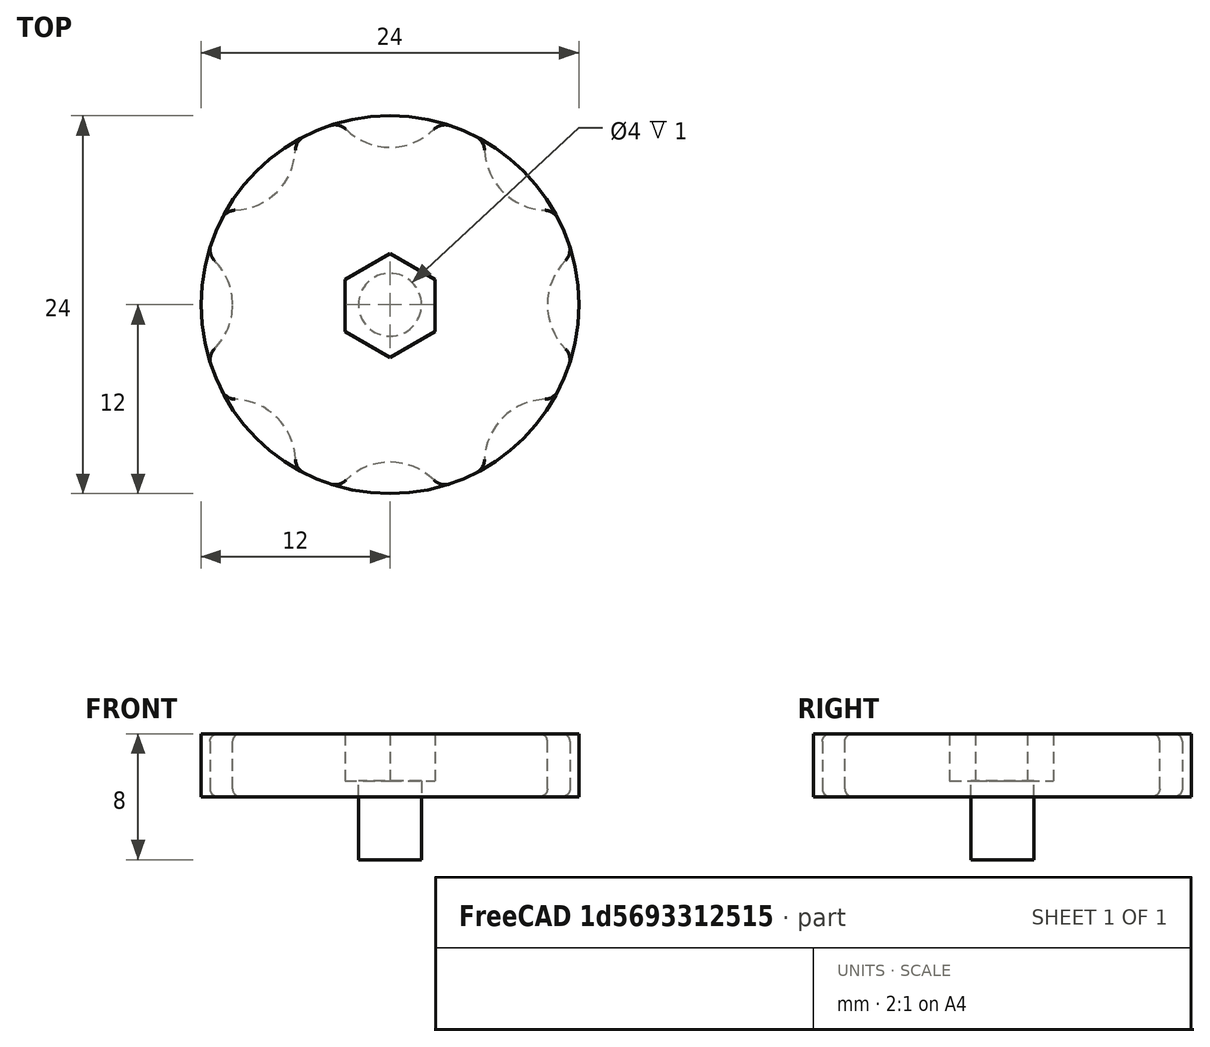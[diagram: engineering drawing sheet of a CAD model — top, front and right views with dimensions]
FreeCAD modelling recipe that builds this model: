
FCSTD DOCUMENT  (FreeCAD 0.15R4671 (Git))
Label: BedKnob
License: All rights reserved
LicenseURL: http://en.wikipedia.org/wiki/All_rights_reserved
objects: Sketcher::SketchObject×4, PartDesign::Pocket×3, PartDesign::Fillet×2, Mesh::Feature×1, PartDesign::Pad×1
note: 14 computed .brp shape members not serialized (recipe doc carries the construction recipe); baked Part::Feature solids carry a one-line shape summary decoded from their .brp

FEATURE [Mesh::Feature] HexNutStyle1_M3
  Placement = pos=(14.2,22,-115) rot=(0,0,1;0rad)
FEATURE [Sketcher::SketchObject] Sketch
  sketch-geometry (1):
    g0: Circle CenterX=0 CenterY=0 CenterZ=0 NormalX=0 NormalY=0 NormalZ=1 Radius=12
  constraints (1):
    c: Radius(g0) = 12
FEATURE [PartDesign::Pad] Pad
  Length = 4
  Length2 = 100
  Sketch = -> Sketch
  Type = 0
FEATURE [Sketcher::SketchObject] Sketch001
  Placement = pos=(0,0,4) rot=(0,0,1;0rad)
  Support = -> Pad [Face3]
  sketch-geometry (7):
    g0: LineSegment StartX=0 StartY=3.25 StartZ=0 EndX=-2.86084 EndY=1.59829 EndZ=0
    g1: LineSegment StartX=-2.86084 StartY=1.59829 StartZ=0 EndX=-2.86084 EndY=-1.70512 EndZ=0
    g2: LineSegment StartX=-2.86084 StartY=-1.70512 StartZ=0 EndX=0 EndY=-3.35682 EndZ=0
    g3: LineSegment StartX=0 StartY=-3.35682 StartZ=0 EndX=2.86084 EndY=-1.70512 EndZ=0
    g4: LineSegment StartX=2.86084 StartY=-1.70512 StartZ=0 EndX=2.86084 EndY=1.59829 EndZ=0
    g5: LineSegment StartX=2.86084 StartY=1.59829 StartZ=0 EndX=0 EndY=3.25 EndZ=0
    g6: Circle [constr] CenterX=0 CenterY=-0.0534101 CenterZ=0 NormalX=0 NormalY=0 NormalZ=1 Radius=3.30341
  constraints (13):
    c: Coincident(g0,g1)
    c: Coincident(g1,g2)
    c: Coincident(g2,g3)
    c: Coincident(g3,g4)
    c: Coincident(g4,g5)
    c: Coincident(g5,g0)
    c: Equal(g0, g1-g5) x5
    c: PointOnObject(g0,g6)
    c: PointOnObject(g1,g6)
    c: PointOnObject(g2,g6)
    c: PointOnObject(g3,g6)
    c: PointOnObject(g4,g6)
    c: PointOnObject(g5,g6)
FEATURE [PartDesign::Pocket] Pocket
  Length = 3
  Sketch = -> Sketch001
  Type = 0
FEATURE [Sketcher::SketchObject] Sketch002
  Placement = pos=(0,0,1) rot=(0,0,1;0rad)
  Support = -> Pocket [Face10]
  sketch-geometry (1):
    g0: Circle CenterX=0 CenterY=0 CenterZ=0 NormalX=0 NormalY=0 NormalZ=1 Radius=2
  constraints (1):
    c: Radius(g0) = 2
FEATURE [PartDesign::Pocket] Pocket001
  Length = 5
  Sketch = -> Sketch002
  Type = 0
FEATURE [Sketcher::SketchObject] Sketch003
  Placement = pos=(0,0,4) rot=(0,0,1;0rad)
  Support = -> Pocket001 [Face3]
  sketch-geometry (8):
    g0: Circle CenterX=0 CenterY=14 CenterZ=0 NormalX=0 NormalY=0 NormalZ=1 Radius=4
    g1: Circle CenterX=14 CenterY=0 CenterZ=0 NormalX=0 NormalY=0 NormalZ=1 Radius=4
    g2: Circle CenterX=0 CenterY=-14 CenterZ=0 NormalX=0 NormalY=0 NormalZ=1 Radius=4
    g3: Circle CenterX=-14 CenterY=0 CenterZ=0 NormalX=0 NormalY=0 NormalZ=1 Radius=4
    g4: Circle CenterX=-10 CenterY=10 CenterZ=0 NormalX=0 NormalY=0 NormalZ=1 Radius=4
    g5: Circle CenterX=10 CenterY=10 CenterZ=0 NormalX=0 NormalY=0 NormalZ=1 Radius=4
    g6: Circle CenterX=-10 CenterY=-10 CenterZ=0 NormalX=0 NormalY=0 NormalZ=1 Radius=4
    g7: Circle CenterX=10 CenterY=-10 CenterZ=0 NormalX=0 NormalY=0 NormalZ=1 Radius=4
  constraints (8):
    c: Radius(g7) = 4
    c: Equal(g7,g1)
    c: Equal(g7,g5)
    c: Equal(g7,g0)
    c: Equal(g7,g4)
    c: Equal(g7,g3)
    c: Equal(g7,g6)
    c: Equal(g7,g2)
FEATURE [PartDesign::Pocket] Pocket002
  Length = 5
  Sketch = -> Sketch003
  Type = 1
FEATURE [PartDesign::Fillet] Fillet
  Base = -> Pocket002 [Edge53,Edge54,Edge52,Edge56,Edge55,Edge58,Edge57,Edge59,Edge60,Edge61,Edge49,Edge4,Edge2,Edge25,Edge50,Edge51]
  Radius = 1
FEATURE [PartDesign::Fillet] Fillet001  label="BedKnob"
  Base = -> Fillet [Edge71,Edge36]
  Radius = 0.5
